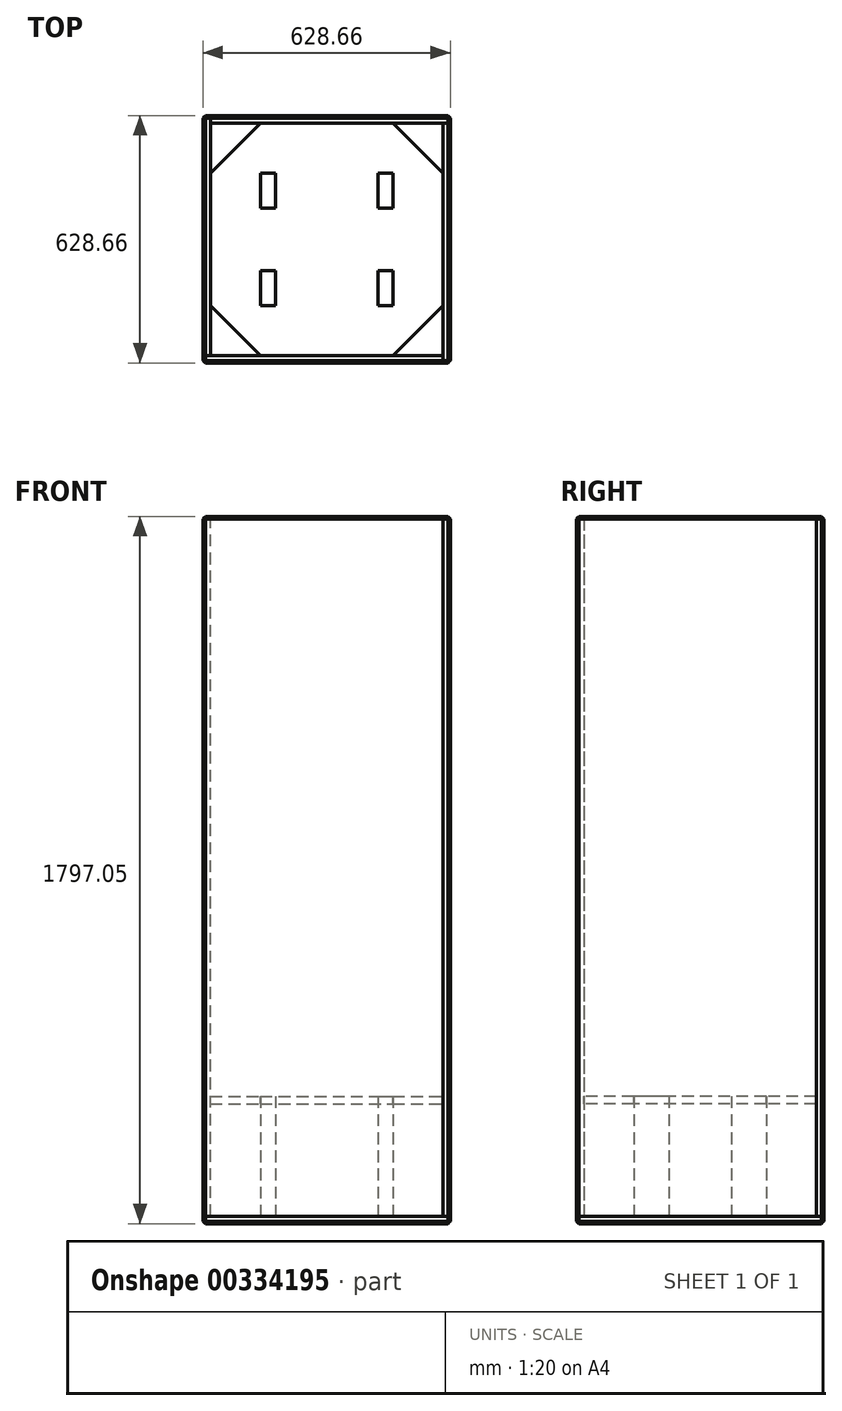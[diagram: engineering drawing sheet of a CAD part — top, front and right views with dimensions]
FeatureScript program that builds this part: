
annotation { "Feature Type Name" : "Feature", "Feature Type Description" : "" }
export const myFeature = defineFeature(function(context is Context, id is Id, definition is map)
    precondition{}
    {
        {
            var Q0;
            Q0=qCreatedBy(makeId("Top.planeOp"),FACE);
            var sketch = newSketch(context, id + "F0", { "sketchPlane" : qUnion([Q0])});
            skLineSegment(sketch, "E0.bottom", {"start": v(307.98, -314.33) * mm, "end": v(-307.97, -314.33) * mm});
            skLineSegment(sketch, "E0.top", {"start": v(307.98, 314.33) * mm, "end": v(-307.98, 314.33) * mm});
            skLineSegment(sketch, "E0.left", {"start": v(314.33, -307.97) * mm, "end": v(314.33, 307.98) * mm});
            skLineSegment(sketch, "E0.right", {"start": v(-314.33, -307.98) * mm, "end": v(-314.33, 307.97) * mm});
            skPoint(sketch, "E0.middle", {"position": v(0, 0) * mm});
            skLineSegment(sketch, "E1", {"start": v(-314.33, 307.97) * mm, "end": v(-307.98, 314.32) * mm});
            skPoint(sketch, "E2.orphan", {"position": v(-314.33, 314.32) * mm});
            skLineSegment(sketch, "E3", {"start": v(307.97, 314.33) * mm, "end": v(314.33, 307.98) * mm});
            skPoint(sketch, "E4.orphan", {"position": v(314.33, 314.33) * mm});
            skLineSegment(sketch, "E5", {"start": v(307.98, -314.33) * mm, "end": v(314.33, -307.97) * mm});
            skPoint(sketch, "E6.orphan", {"position": v(314.33, -314.33) * mm});
            skLineSegment(sketch, "E7", {"start": v(-314.32, -307.98) * mm, "end": v(-307.97, -314.33) * mm});
            skPoint(sketch, "E8.orphan", {"position": v(-314.33, -314.33) * mm});
            skSolve(sketch);
        }
        {
            var Q0;
            Q0 = qSketchRegion(id + "F0", true);
            extrude(context, id + "F1", {"entities" : qUnion([Q0]), "oppositeDirection" : true, "depth" : 19.05 * mm});
        }
        {
            var Q0;
            Q0=makeQuery(id+"F1.opExtrude","SWEPT_FACE",FACE,{"disambiguationData":[OSD([sQuery(id+"F0.wireOp",EDGE,"E0.left")])]});
            var sketch = newSketch(context, id + "F2", { "sketchPlane" : qUnion([Q0])});
            skLineSegment(sketch, "E9.bottom", {"start": v(-314.33, 0) * mm, "end": v(295.28, 0) * mm});
            skLineSegment(sketch, "E9.top", {"start": v(-307.98, 1778) * mm, "end": v(295.27, 1778) * mm});
            skLineSegment(sketch, "E9.left", {"start": v(-314.33, 0) * mm, "end": v(-314.33, 1771.65) * mm});
            skLineSegment(sketch, "E9.right", {"start": v(295.28, 0) * mm, "end": v(295.27, 1778) * mm});
            skLineSegment(sketch, "E10", {"start": v(-314.33, 1771.65) * mm, "end": v(-307.98, 1778) * mm});
            skPoint(sketch, "E11.orphan", {"position": v(-314.33, 1778) * mm});
            skSolve(sketch);
        }
        {
            var Q0;
            Q0 = qSketchRegion(id + "F2", true);
            extrude(context, id + "F3", {"entities" : qUnion([Q0]), "oppositeDirection" : true, "depth" : 19.05 * mm});
        }
        {
            var Q0;
            Q0=makeQuery(id+"F1.opExtrude","SWEPT_FACE",FACE,{"disambiguationData":[OSD([sQuery(id+"F0.wireOp",EDGE,"E0.top")])]});
            var sketch = newSketch(context, id + "F4", { "sketchPlane" : qUnion([Q0])});
            skLineSegment(sketch, "E12.bottom", {"start": v(-314.33, 0) * mm, "end": v(295.28, 0) * mm});
            skLineSegment(sketch, "E12.top", {"start": v(-307.98, 1778) * mm, "end": v(295.27, 1778) * mm});
            skLineSegment(sketch, "E12.left", {"start": v(-314.33, 0) * mm, "end": v(-314.33, 1771.65) * mm});
            skLineSegment(sketch, "E12.right", {"start": v(295.28, 0) * mm, "end": v(295.27, 1778) * mm});
            skLineSegment(sketch, "E13", {"start": v(-314.33, 1771.65) * mm, "end": v(-307.98, 1778) * mm});
            skPoint(sketch, "E14.orphan", {"position": v(-314.33, 1778) * mm});
            skSolve(sketch);
        }
        {
            var Q0;
            Q0 = qSketchRegion(id + "F4", true);
            extrude(context, id + "F5", {"entities" : qUnion([Q0]), "oppositeDirection" : true, "depth" : 19.05 * mm});
        }
        {
            var Q0;
            Q0=makeQuery(id+"F1.opExtrude","SWEPT_FACE",FACE,{"disambiguationData":[OSD([sQuery(id+"F0.wireOp",EDGE,"E0.bottom")])]});
            var sketch = newSketch(context, id + "F6", { "sketchPlane" : qUnion([Q0])});
            skLineSegment(sketch, "E15.bottom", {"start": v(-307.98, 1778) * mm, "end": v(295.27, 1778) * mm});
            skLineSegment(sketch, "E15.top", {"start": v(-314.33, 0) * mm, "end": v(295.27, 0) * mm});
            skLineSegment(sketch, "E15.left", {"start": v(-314.33, 1771.65) * mm, "end": v(-314.33, 0) * mm});
            skLineSegment(sketch, "E15.right", {"start": v(295.27, 1778) * mm, "end": v(295.27, 0) * mm});
            skLineSegment(sketch, "E16", {"start": v(-314.33, 1771.65) * mm, "end": v(-307.98, 1778) * mm});
            skPoint(sketch, "E17.orphan", {"position": v(-314.33, 1778) * mm});
            skSolve(sketch);
        }
        {
            var Q0;
            Q0 = qSketchRegion(id + "F6", true);
            extrude(context, id + "F7", {"entities" : qUnion([Q0]), "oppositeDirection" : true, "depth" : 19.05 * mm});
        }
        {
            var Q0;
            Q0=makeQuery(id+"F1.opExtrude","SWEPT_FACE",FACE,{"disambiguationData":[OSD([sQuery(id+"F0.wireOp",EDGE,"E0.right")])]});
            var sketch = newSketch(context, id + "F8", { "sketchPlane" : qUnion([Q0])});
            skLineSegment(sketch, "E18.bottom", {"start": v(-307.98, 1778) * mm, "end": v(295.27, 1778) * mm});
            skLineSegment(sketch, "E18.top", {"start": v(-314.33, 0) * mm, "end": v(295.28, 0) * mm});
            skLineSegment(sketch, "E18.left", {"start": v(-314.33, 1771.65) * mm, "end": v(-314.33, 0) * mm});
            skLineSegment(sketch, "E18.right", {"start": v(295.27, 1778) * mm, "end": v(295.28, 0) * mm});
            skLineSegment(sketch, "E19", {"start": v(-314.33, 1771.65) * mm, "end": v(-307.98, 1778) * mm});
            skPoint(sketch, "E20.orphan", {"position": v(-314.33, 1778) * mm});
            skSolve(sketch);
        }
        {
            var Q0;
            Q0 = qSketchRegion(id + "F8", true);
            extrude(context, id + "F9", {"entities" : qUnion([Q0]), "oppositeDirection" : true, "depth" : 19.05 * mm});
        }
        {
            var Q0;
            Q0=makeQuery(id+"F7.opExtrude","CAP_EDGE",EDGE,{"disambiguationData":[OSD([sQuery(id+"F6.wireOp",EDGE,"E15.bottom")])],"isStart":true});
            var Q1;
            Q1=makeQuery(id+"F3.opExtrude","CAP_EDGE",EDGE,{"disambiguationData":[OSD([sQuery(id+"F2.wireOp",EDGE,"E9.top")])],"isStart":true});
            var Q2;
            Q2=makeQuery(id+"F5.opExtrude","CAP_EDGE",EDGE,{"disambiguationData":[OSD([sQuery(id+"F4.wireOp",EDGE,"E12.top")])],"isStart":true});
            var Q3;
            Q3=makeQuery(id+"F9.opExtrude","CAP_EDGE",EDGE,{"disambiguationData":[OSD([sQuery(id+"F8.wireOp",EDGE,"E18.bottom")])],"isStart":true});
            chamfer(context, id + "F10", {"entities" : qUnion([Q0, Q1, Q2, Q3]), "width" : 6.35 * mm, "tangentPropagation" : true});
        }
        {
            var Q0;
            Q0=makeQuery(id+"F3.opExtrude","CAP_EDGE",EDGE,{"disambiguationData":[OSD([sQuery(id+"F2.wireOp",EDGE,"E9.left")])],"isStart":true});
            chamfer(context, id + "F11", {"entities" : qUnion([Q0]), "width" : 6.35 * mm, "tangentPropagation" : true});
        }
        {
            var Q0;
            Q0=makeQuery(id+"F7.opExtrude","CAP_EDGE",EDGE,{"disambiguationData":[OSD([sQuery(id+"F6.wireOp",EDGE,"E15.left")])],"isStart":true});
            chamfer(context, id + "F12", {"entities" : qUnion([Q0]), "width" : 6.35 * mm, "tangentPropagation" : true});
        }
        {
            var Q0;
            Q0=makeQuery(id+"F5.opExtrude","CAP_EDGE",EDGE,{"disambiguationData":[OSD([sQuery(id+"F4.wireOp",EDGE,"E12.left")])],"isStart":true});
            chamfer(context, id + "F13", {"entities" : qUnion([Q0]), "width" : 6.35 * mm, "tangentPropagation" : true});
        }
        {
            var Q0;
            Q0=makeQuery(id+"F9.opExtrude","CAP_EDGE",EDGE,{"disambiguationData":[OSD([sQuery(id+"F8.wireOp",EDGE,"E18.left")])],"isStart":true});
            chamfer(context, id + "F14", {"entities" : qUnion([Q0]), "width" : 6.35 * mm, "tangentPropagation" : true});
        }
        {
            var Q0;
            Q0=makeQuery(id+"F1.opExtrude","CAP_EDGE",EDGE,{"disambiguationData":[OSD([sQuery(id+"F0.wireOp",EDGE,"E0.bottom")])],"isStart":false});
            var Q1;
            Q1=makeQuery(id+"F1.opExtrude","CAP_EDGE",EDGE,{"disambiguationData":[OSD([sQuery(id+"F0.wireOp",EDGE,"E0.left")])],"isStart":false});
            var Q2;
            Q2=makeQuery(id+"F1.opExtrude","CAP_EDGE",EDGE,{"disambiguationData":[OSD([sQuery(id+"F0.wireOp",EDGE,"E0.top")])],"isStart":false});
            var Q3;
            Q3=makeQuery(id+"F1.opExtrude","CAP_EDGE",EDGE,{"disambiguationData":[OSD([sQuery(id+"F0.wireOp",EDGE,"E0.right")])],"isStart":false});
            chamfer(context, id + "F15", {"entities" : qUnion([Q0, Q1, Q2, Q3]), "width" : 6.35 * mm, "tangentPropagation" : true});
        }
        {
            var Q0;
            Q0=makeQuery(id+"F0.imprint","IMPRINT",FACE,{"disambiguationData":[TD([[makeQuery(id+"F0.imprint","IMPRINT",EDGE,{"derivedFrom":sQuery(id+"F0.wireOp",EDGE,"E0.bottom")}),-1.0]])]});
            var sketch = newSketch(context, id + "F16", { "sketchPlane" : qUnion([Q0])});
            skLineSegment(sketch, "E21.bottom", {"start": v(-168.28, 168.28) * mm, "end": v(-130.18, 168.28) * mm});
            skLineSegment(sketch, "E21.top", {"start": v(-168.28, 79.38) * mm, "end": v(-130.18, 79.38) * mm});
            skLineSegment(sketch, "E21.left", {"start": v(-168.28, 168.28) * mm, "end": v(-168.28, 79.38) * mm});
            skLineSegment(sketch, "E21.right", {"start": v(-130.18, 168.28) * mm, "end": v(-130.18, 79.37) * mm});
            skLineSegment(sketch, "E22.bottom", {"start": v(130.18, 168.28) * mm, "end": v(168.28, 168.28) * mm});
            skLineSegment(sketch, "E22.top", {"start": v(130.18, 79.38) * mm, "end": v(168.28, 79.38) * mm});
            skLineSegment(sketch, "E22.left", {"start": v(130.18, 168.28) * mm, "end": v(130.18, 79.38) * mm});
            skLineSegment(sketch, "E22.right", {"start": v(168.28, 168.28) * mm, "end": v(168.28, 79.38) * mm});
            skLineSegment(sketch, "E23.bottom", {"start": v(-168.28, -79.38) * mm, "end": v(-130.18, -79.38) * mm});
            skLineSegment(sketch, "E23.top", {"start": v(-168.28, -168.28) * mm, "end": v(-130.18, -168.28) * mm});
            skLineSegment(sketch, "E23.left", {"start": v(-168.28, -79.38) * mm, "end": v(-168.28, -168.28) * mm});
            skLineSegment(sketch, "E23.right", {"start": v(-130.18, -79.38) * mm, "end": v(-130.18, -168.28) * mm});
            skLineSegment(sketch, "E24.bottom", {"start": v(130.17, -79.38) * mm, "end": v(168.27, -79.38) * mm});
            skLineSegment(sketch, "E24.top", {"start": v(130.17, -168.28) * mm, "end": v(168.27, -168.28) * mm});
            skLineSegment(sketch, "E24.left", {"start": v(130.17, -79.38) * mm, "end": v(130.17, -168.28) * mm});
            skLineSegment(sketch, "E24.right", {"start": v(168.27, -79.38) * mm, "end": v(168.27, -168.28) * mm});
            skSolve(sketch);
        }
        {
            var Q0;
            Q0 = qSketchRegion(id + "F16", true);
            extrude(context, id + "F17", {"entities" : qUnion([Q0]), "operationType" : NewBodyOperationType.ADD, "depth" : 304.8 * mm});
        }
        {
            var Q0;
            Q0=makeQuery(id+"F17.opExtrude","CAP_FACE",FACE,{"disambiguationData":[OSD([sQuery(id+"F16.wireOp",EDGE,"E21.bottom"),sQuery(id+"F16.wireOp",EDGE,"E21.top"),sQuery(id+"F16.wireOp",EDGE,"E21.left"),sQuery(id+"F16.wireOp",EDGE,"E21.right")])],"isStart":false});
            var sketch = newSketch(context, id + "F18", { "sketchPlane" : qUnion([Q0])});
            skLineSegment(sketch, "E25.bottom", {"start": v(-168.27, 295.28) * mm, "end": v(168.28, 295.28) * mm});
            skLineSegment(sketch, "E25.top", {"start": v(-168.27, -295.28) * mm, "end": v(168.28, -295.28) * mm});
            skLineSegment(sketch, "E25.left", {"start": v(-295.27, 168.28) * mm, "end": v(-295.27, -168.28) * mm});
            skLineSegment(sketch, "E25.right", {"start": v(295.28, 168.28) * mm, "end": v(295.28, -168.28) * mm});
            skLineSegment(sketch, "E26", {"start": v(-295.27, 168.28) * mm, "end": v(-168.27, 295.28) * mm});
            skLineSegment(sketch, "E27", {"start": v(168.28, 295.28) * mm, "end": v(295.28, 168.28) * mm});
            skLineSegment(sketch, "E28", {"start": v(295.28, -168.28) * mm, "end": v(168.28, -295.28) * mm});
            skLineSegment(sketch, "E29", {"start": v(-295.27, -168.28) * mm, "end": v(-168.27, -295.28) * mm});
            skPoint(sketch, "E30.orphan", {"position": v(-295.27, 295.28) * mm});
            skPoint(sketch, "E31.orphan", {"position": v(295.28, 295.27) * mm});
            skPoint(sketch, "E32.orphan", {"position": v(295.27, -295.28) * mm});
            skPoint(sketch, "E33.orphan", {"position": v(-295.27, -295.28) * mm});
            skSolve(sketch);
        }
        {
            var Q0;
            Q0 = qSketchRegion(id + "F18", true);
            extrude(context, id + "F19", {"entities" : qUnion([Q0]), "oppositeDirection" : true, "depth" : 19.05 * mm});
        }
    });
